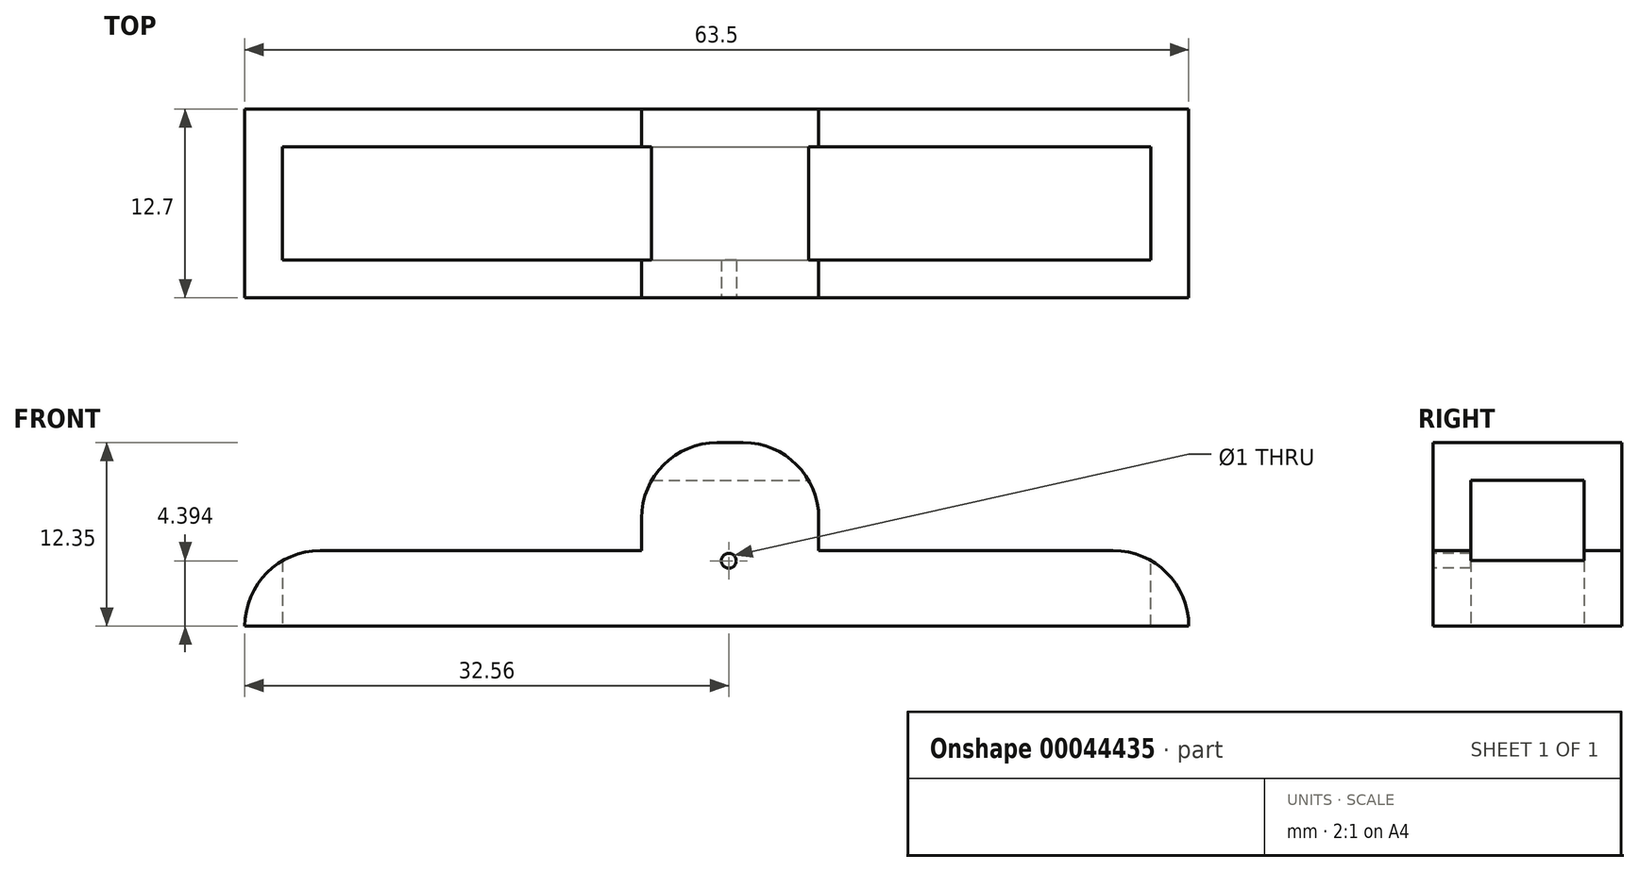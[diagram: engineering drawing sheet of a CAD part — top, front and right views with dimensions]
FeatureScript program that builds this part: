
annotation { "Feature Type Name" : "Feature", "Feature Type Description" : "" }
export const myFeature = defineFeature(function(context is Context, id is Id, definition is map)
    precondition{}
    {
        {
            var Q0;
            Q0=qCreatedBy(makeId("Front.planeOp"),FACE);
            var sketch = newSketch(context, id + "F0", { "sketchPlane" : qUnion([Q0])});
            skLineSegment(sketch, "E0", {"start": v(0, 0) * mm, "end": v(28.4, 0) * mm});
            skLineSegment(sketch, "E1", {"start": v(28.4, 0) * mm, "end": v(28.4, 5.08) * mm});
            skLineSegment(sketch, "E2", {"start": v(28.4, 5.08) * mm, "end": v(-30.02, 5.08) * mm});
            skLineSegment(sketch, "E3", {"start": v(-30.02, 5.08) * mm, "end": v(-30.02, 0) * mm});
            skLineSegment(sketch, "E4", {"start": v(-30.02, 0) * mm, "end": v(0, 0) * mm});
            skLineSegment(sketch, "E5", {"start": v(-5.87, 0) * mm, "end": v(-5.87, 9.8) * mm});
            skLineSegment(sketch, "E6", {"start": v(-5.87, 9.8) * mm, "end": v(6.05, 9.8) * mm});
            skLineSegment(sketch, "E7", {"start": v(6.05, 9.8) * mm, "end": v(6.05, 0) * mm});
            skLineSegment(sketch, "E8", {"start": v(0, 9.8) * mm, "end": v(0, 4.35) * mm});
            skSolve(sketch);
        }
        {
            var Q0;
            Q0 = qSketchRegion(id + "F0", true);
            extrude(context, id + "F1", {"entities" : qUnion([Q0]), "depth" : 7.62 * mm});
        }
        {
            var Q0;
            {var subQ0=sQuery(id+"F0.wireOp",EDGE,"E2");Q0=makeQuery(id+"F1.opExtrude","SWEPT_FACE",FACE,{"disambiguationData":[OSD([subQ0]),TDD([makeQuery(id+"F0.imprint","IMPRINT",EDGE,{"disambiguationData":[TD([[makeQuery(id+"F0.imprint","INTERSECT",VERTEX,{"derivedFrom":[subQ0,sQuery(id+"F0.wireOp",EDGE,"E3")]}),1.0]])],"derivedFrom":subQ0})])]});}
            var Q1;
            Q1=makeQuery(id+"F1.opExtrude","SWEPT_FACE",FACE,{"disambiguationData":[OSD([sQuery(id+"F0.wireOp",EDGE,"E0"),sQuery(id+"F0.wireOp",EDGE,"E4")])]});
            var Q2;
            {var subQ0=sQuery(id+"F0.wireOp",EDGE,"E2");Q2=makeQuery(id+"F1.opExtrude","SWEPT_FACE",FACE,{"disambiguationData":[OSD([subQ0]),TDD([makeQuery(id+"F0.imprint","IMPRINT",EDGE,{"disambiguationData":[TD([[makeQuery(id+"F0.imprint","INTERSECT",VERTEX,{"derivedFrom":[sQuery(id+"F0.wireOp",EDGE,"E1"),subQ0]}),-1.0]])],"derivedFrom":subQ0})])]});}
            var Q3;
            Q3=makeQuery(id+"F1.opExtrude","SWEPT_FACE",FACE,{"disambiguationData":[OSD([sQuery(id+"F0.wireOp",EDGE,"E7")])]});
            var Q4;
            Q4=makeQuery(id+"F1.opExtrude","SWEPT_FACE",FACE,{"disambiguationData":[OSD([sQuery(id+"F0.wireOp",EDGE,"E5")])]});
            shell(context, id + "F2", {"entities" : qUnion([Q0, Q1, Q2, Q3, Q4]), "thickness" : 2.54 * mm, "oppositeDirection" : true});
        }
        {
            var Q0;
            Q0=makeQuery(id+"F1.opExtrude","CAP_FACE",FACE,{"disambiguationData":[OSD([sQuery(id+"F0.wireOp",EDGE,"E0"),sQuery(id+"F0.wireOp",EDGE,"E1"),sQuery(id+"F0.wireOp",EDGE,"E2"),sQuery(id+"F0.wireOp",EDGE,"E3"),sQuery(id+"F0.wireOp",EDGE,"E4"),sQuery(id+"F0.wireOp",EDGE,"E5"),sQuery(id+"F0.wireOp",EDGE,"E6"),sQuery(id+"F0.wireOp",EDGE,"E7")])],"isStart":false});
            var sketch = newSketch(context, id + "F3", { "sketchPlane" : qUnion([Q0])});
            skCircle(sketch, "E9", {"center": v(0, 4.4) * mm, "radius": 0.5 * mm});
            skSolve(sketch);
        }
        {
            var Q0;
            Q0 = qSketchRegion(id + "F3", true);
            extrude(context, id + "F4", {"entities" : qUnion([Q0]), "operationType" : NewBodyOperationType.REMOVE, "oppositeDirection" : true, "depth" : 8.1 * mm});
        }
        {
            var Q0;
            Q0=makeQuery(id+"F1.opExtrude","SWEPT_EDGE",EDGE,{"disambiguationData":[OSD([sQuery(id+"F0.wireOp",EDGE,"E2"),sQuery(id+"F0.wireOp",EDGE,"E3")])]});
            var Q1;
            Q1=makeQuery(id+"F1.opExtrude","SWEPT_EDGE",EDGE,{"disambiguationData":[OSD([sQuery(id+"F0.wireOp",EDGE,"E1"),sQuery(id+"F0.wireOp",EDGE,"E2")])]});
            fillet(context, id + "F5", {"entities" : qUnion([Q0, Q1]), "radius" : 5.08 * mm, "tangentPropagation" : true, "allowEdgeOverflow" : false});
        }
        {
            var Q0;
            Q0=makeQuery(id+"F1.opExtrude","SWEPT_EDGE",EDGE,{"disambiguationData":[OSD([sQuery(id+"F0.wireOp",EDGE,"E5"),sQuery(id+"F0.wireOp",EDGE,"E6")])]});
            var Q1;
            Q1=makeQuery(id+"F1.opExtrude","SWEPT_EDGE",EDGE,{"disambiguationData":[OSD([sQuery(id+"F0.wireOp",EDGE,"E6"),sQuery(id+"F0.wireOp",EDGE,"E7")])]});
            fillet(context, id + "F6", {"entities" : qUnion([Q0, Q1]), "radius" : 5.08 * mm, "tangentPropagation" : true, "allowEdgeOverflow" : false});
        }
        {
            var Q0;
            Q0 = qSketchRegion(id + "F3", true);
            extrude(context, id + "F7", {"entities" : qUnion([Q0]), "operationType" : NewBodyOperationType.REMOVE, "oppositeDirection" : true, "depth" : 7.36 * mm});
        }
    });
